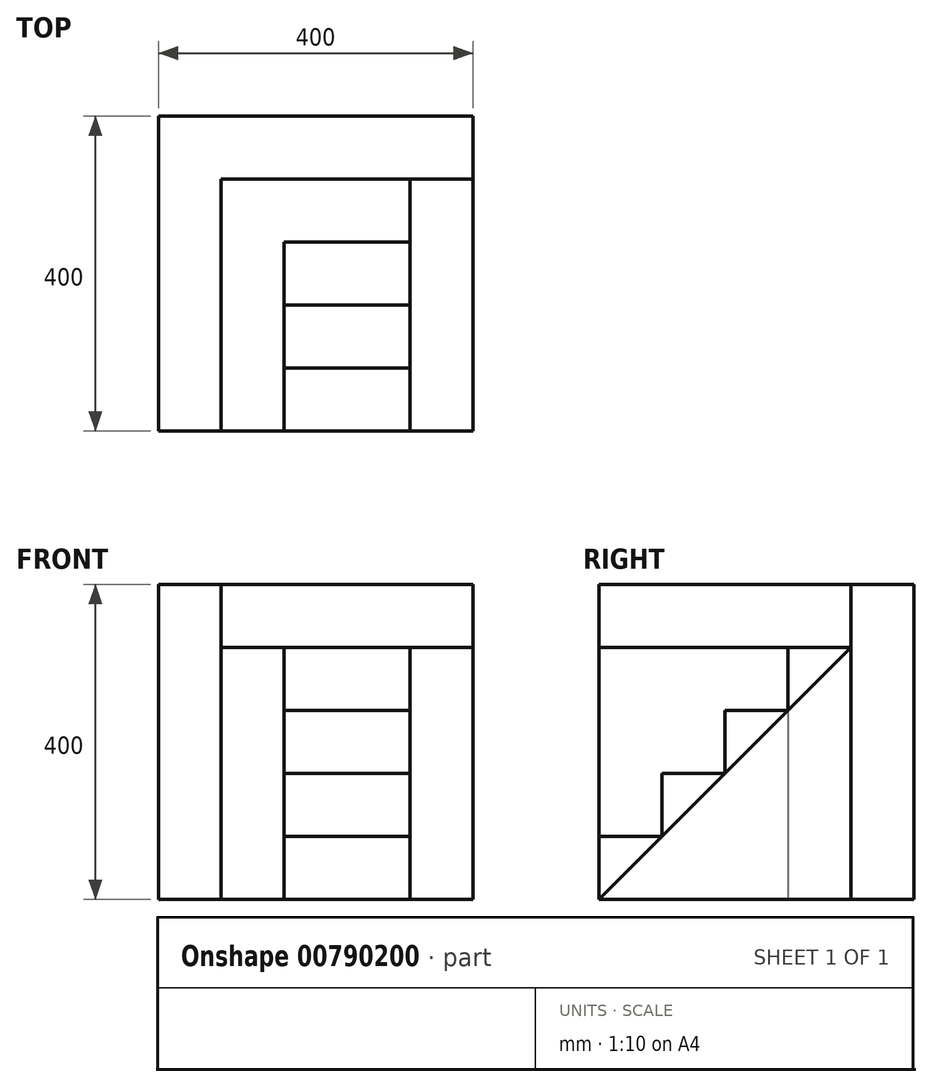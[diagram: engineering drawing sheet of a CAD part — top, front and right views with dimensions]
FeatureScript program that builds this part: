
annotation { "Feature Type Name" : "Feature", "Feature Type Description" : "" }
export const myFeature = defineFeature(function(context is Context, id is Id, definition is map)
    precondition{}
    {
        {
            var Q0;
            Q0=qCreatedBy(makeId("Top.planeOp"),FACE);
            var sketch = newSketch(context, id + "F0", { "sketchPlane" : qUnion([Q0])});
            skLineSegment(sketch, "E0.bottom", {"start": v(-200, 200) * mm, "end": v(200, 200) * mm});
            skLineSegment(sketch, "E0.top", {"start": v(-200, -200) * mm, "end": v(200, -200) * mm});
            skLineSegment(sketch, "E0.left", {"start": v(-200, 200) * mm, "end": v(-200, -200) * mm});
            skLineSegment(sketch, "E0.right", {"start": v(200, 200) * mm, "end": v(200, -200) * mm});
            skPoint(sketch, "E0.middle", {"position": v(0, 0) * mm});
            skLineSegment(sketch, "E1", {"start": v(-120, 120) * mm, "end": v(-120, -200) * mm});
            skLineSegment(sketch, "E2", {"start": v(200, 120) * mm, "end": v(-120, 120) * mm});
            skLineSegment(sketch, "E3", {"start": v(-40, -200) * mm, "end": v(-40, 40) * mm});
            skLineSegment(sketch, "E4", {"start": v(120, -200) * mm, "end": v(120, 120) * mm});
            skLineSegment(sketch, "E5", {"start": v(120, 40) * mm, "end": v(-40, 40) * mm});
            skPoint(sketch, "E6.orphan", {"position": v(200, 40) * mm});
            skLineSegment(sketch, "E7", {"start": v(120, -40) * mm, "end": v(-40, -40) * mm});
            skLineSegment(sketch, "E8", {"start": v(120, -120) * mm, "end": v(-40, -120) * mm});
            skPoint(sketch, "E9.orphan", {"position": v(200, -40) * mm});
            skPoint(sketch, "E10.orphan", {"position": v(200, -120) * mm});
            skSolve(sketch);
        }
        {
            var Q0;
            {var subQ1=sQuery(id+"F0.wireOp",EDGE,"E0.bottom");Q0=makeQuery(id+"F0.imprint","IMPRINT",FACE,{"disambiguationData":[TD([[makeQuery(id+"F0.imprint","IMPRINT",EDGE,{"derivedFrom":subQ1}),-1.0]])]});}
            extrude(context, id + "F1", {"entities" : qUnion([Q0]), "depth" : 400 * mm, "offsetDistance" : 25 * mm});
        }
        {
            var Q0;
            {var subQ5=sQuery(id+"F0.wireOp",EDGE,"E8");Q0=makeQuery(id+"F0.imprint","IMPRINT",FACE,{"disambiguationData":[TD([[makeQuery(id+"F0.imprint","IMPRINT",EDGE,{"derivedFrom":subQ5}),1.0]])]});}
            extrude(context, id + "F2", {"entities" : qUnion([Q0]), "depth" : 80 * mm, "offsetDistance" : 25 * mm});
        }
        {
            var Q0;
            {var subQ0=sQuery(id+"F0.wireOp",EDGE,"E7");Q0=makeQuery(id+"F0.imprint","IMPRINT",FACE,{"disambiguationData":[TD([[makeQuery(id+"F0.imprint","IMPRINT",EDGE,{"derivedFrom":subQ0}),1.0]])]});}
            extrude(context, id + "F3", {"entities" : qUnion([Q0]), "operationType" : NewBodyOperationType.ADD, "depth" : 160 * mm, "offsetDistance" : 25 * mm});
        }
        {
            var Q0;
            {var subQ0=sQuery(id+"F0.wireOp",EDGE,"E5");Q0=makeQuery(id+"F0.imprint","IMPRINT",FACE,{"disambiguationData":[TD([[makeQuery(id+"F0.imprint","IMPRINT",EDGE,{"derivedFrom":subQ0}),1.0]])]});}
            extrude(context, id + "F4", {"entities" : qUnion([Q0]), "operationType" : NewBodyOperationType.ADD, "depth" : 240 * mm, "offsetDistance" : 25 * mm});
        }
        {
            var Q0;
            {var subQ5=sQuery(id+"F0.wireOp",EDGE,"E1");Q0=makeQuery(id+"F0.imprint","IMPRINT",FACE,{"disambiguationData":[TD([[makeQuery(id+"F0.imprint","IMPRINT",EDGE,{"derivedFrom":subQ5}),1.0]])]});}
            extrude(context, id + "F5", {"entities" : qUnion([Q0]), "depth" : 320 * mm, "offsetDistance" : 25 * mm});
        }
        {
            var Q0;
            {var subQ0=sQuery(id+"F0.wireOp",EDGE,"E0.right");var subQ1=sQuery(id+"F0.wireOp",EDGE,"E0.top");var subQ2=makeQuery(id+"F0.imprint","INTERSECT",VERTEX,{"derivedFrom":[subQ1,subQ0]});Q0=makeQuery(id+"F0.imprint","IMPRINT",FACE,{"disambiguationData":[TD([[makeQuery(id+"F0.imprint","IMPRINT",EDGE,{"disambiguationData":[TD([[subQ2,1.0]])],"derivedFrom":subQ1}),1.0]])]});}
            extrude(context, id + "F6", {"entities" : qUnion([Q0]), "depth" : 320 * mm, "offsetDistance" : 25 * mm});
        }
        {
            var Q0;
            Q0=makeQuery(id+"F6.opExtrude","SWEPT_FACE",FACE,{"disambiguationData":[OSD([sQuery(id+"F0.wireOp",EDGE,"E0.right")])]});
            var sketch = newSketch(context, id + "F7", { "sketchPlane" : qUnion([Q0])});
            skLineSegment(sketch, "E11", {"start": v(120, 320) * mm, "end": v(-200, 0) * mm});
            skSolve(sketch);
        }
        {
            var Q0;
            Q0=makeQuery(id+"F7.imprint","IMPRINT",FACE,{"disambiguationData":[TD([[makeQuery(id+"F7.imprint","IMPRINT",EDGE,{"derivedFrom":sQuery(id+"F7.wireOp",EDGE,"E11")}),-1.0]])]});
            extrude(context, id + "F8", {"entities" : qUnion([Q0]), "operationType" : NewBodyOperationType.REMOVE, "oppositeDirection" : true, "depth" : 80 * mm, "offsetDistance" : 25 * mm});
        }
    });
